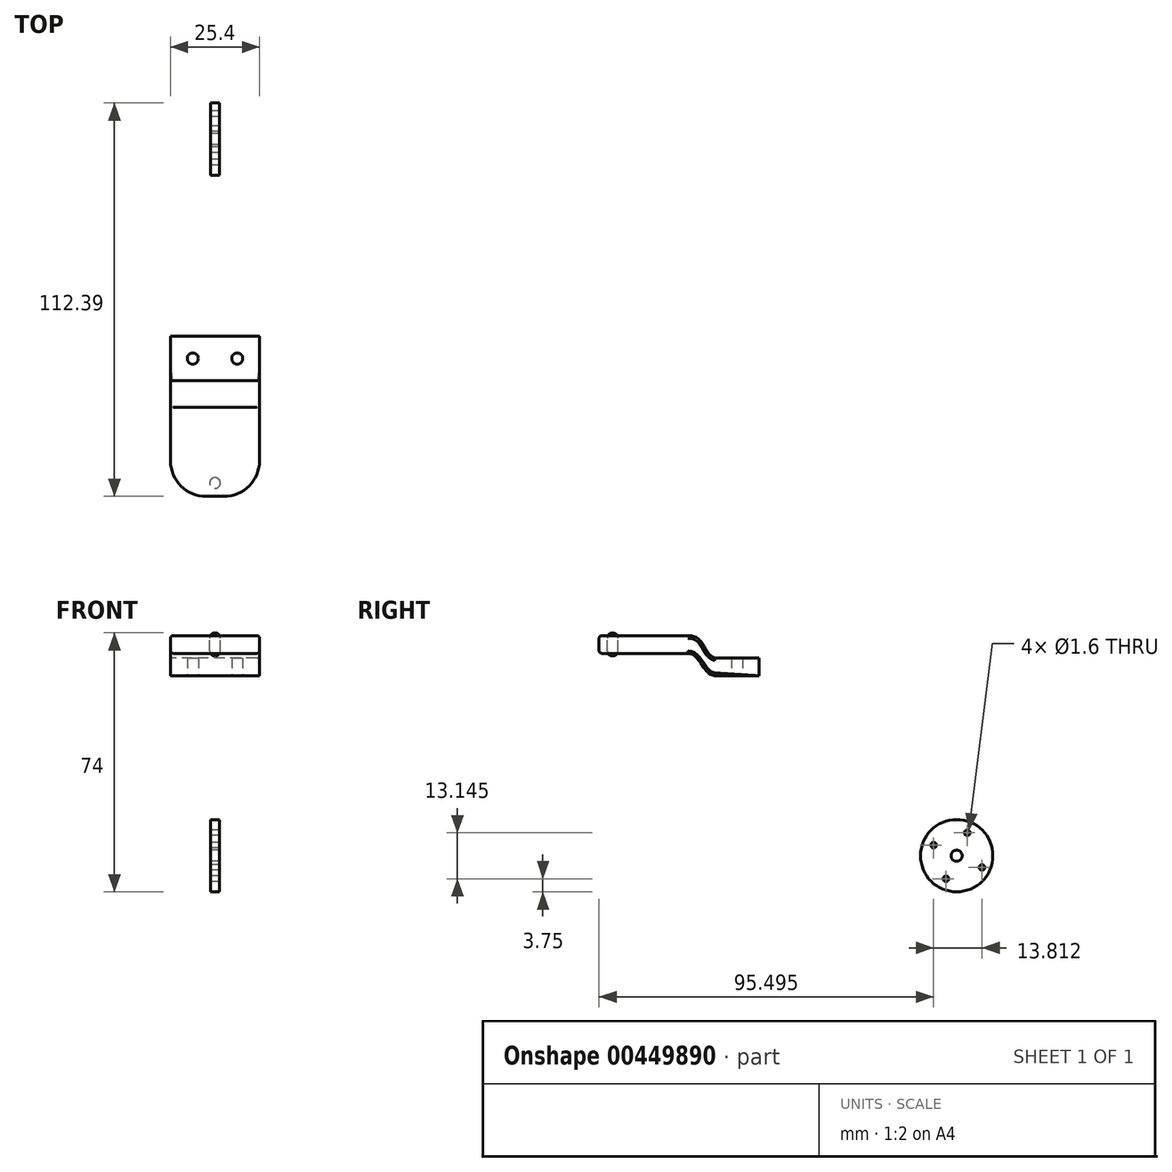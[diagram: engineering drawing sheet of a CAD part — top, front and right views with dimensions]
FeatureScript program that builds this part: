
annotation { "Feature Type Name" : "Feature", "Feature Type Description" : "" }
export const myFeature = defineFeature(function(context is Context, id is Id, definition is map)
    precondition{}
    {
        {
            var Q0;
            Q0=qCreatedBy(makeId("Right.planeOp"),FACE);
            var sketch = newSketch(context, id + "F0", { "sketchPlane" : qUnion([Q0])});
            skLineSegment(sketch, "E0.bottom", {"start": v(-34.21, 26.74) * mm, "end": v(-59.61, 26.74) * mm});
            skLineSegment(sketch, "E0.top", {"start": v(-34.21, 31.82) * mm, "end": v(-59.61, 31.82) * mm});
            skLineSegment(sketch, "E0.left", {"start": v(-34.21, 26.74) * mm, "end": v(-34.21, 31.82) * mm});
            skLineSegment(sketch, "E0.right", {"start": v(-59.61, 26.74) * mm, "end": v(-59.61, 31.82) * mm});
            skPoint(sketch, "E0.middle", {"position": v(-46.91, 29.28) * mm});
            skLineSegment(sketch, "E1.bottom", {"start": v(-13.9, 20.4) * mm, "end": v(-26.6, 20.4) * mm});
            skLineSegment(sketch, "E1.top", {"start": v(-13.9, 25.47) * mm, "end": v(-26.6, 25.47) * mm});
            skLineSegment(sketch, "E1.left", {"start": v(-13.9, 20.4) * mm, "end": v(-13.9, 25.47) * mm});
            skLineSegment(sketch, "E1.right", {"start": v(-26.6, 20.4) * mm, "end": v(-26.6, 25.47) * mm});
            skPoint(sketch, "E1.middle", {"position": v(-20.24, 22.93) * mm});
            skFitSpline(sketch, "E2", {"points": [v(-34.21, 31.82) * mm, v(-26.6, 25.47) * mm], "startDerivative": vector(14.44, 0.2) * mm, "endDerivative": vector(9.5, -2.66) * mm});
            skFitSpline(sketch, "E3", {"points": [v(-34.21, 26.74) * mm, v(-26.6, 20.4) * mm], "startDerivative": vector(10.36, -0.24) * mm, "endDerivative": vector(10.48, -0.64) * mm});
            skSolve(sketch);
        }
        {
            var Q0;
            Q0 = qSketchRegion(id + "F0", true);
            extrude(context, id + "F1", {"entities" : qUnion([Q0]), "endBound" : BoundingType.SYMMETRIC, "depth" : 25.4 * mm});
        }
        {
            var Q0;
            Q0=makeQuery(id+"F1.opExtrude","CAP_EDGE",EDGE,{"disambiguationData":[OSD([sQuery(id+"F0.wireOp",EDGE,"E0.right")])],"isStart":false});
            var Q1;
            Q1=makeQuery(id+"F1.opExtrude","CAP_EDGE",EDGE,{"disambiguationData":[OSD([sQuery(id+"F0.wireOp",EDGE,"E0.right")])],"isStart":true});
            fillet(context, id + "F2", {"entities" : qUnion([Q0, Q1]), "radius" : 10.16 * mm, "tangentPropagation" : true, "allowEdgeOverflow" : false});
        }
        {
            var Q0;
            Q0=makeQuery(id+"F1.opExtrude","CAP_EDGE",EDGE,{"disambiguationData":[OSD([sQuery(id+"F0.wireOp",EDGE,"E0.top")])],"isStart":false});
            var Q1;
            Q1=makeQuery(id+"F1.opExtrude","CAP_EDGE",EDGE,{"disambiguationData":[OSD([sQuery(id+"F0.wireOp",EDGE,"E1.top")])],"isStart":false});
            var Q2;
            Q2=makeQuery(id+"F1.opExtrude","CAP_EDGE",EDGE,{"disambiguationData":[OSD([sQuery(id+"F0.wireOp",EDGE,"E1.top")])],"isStart":true});
            var Q3;
            Q3=makeQuery(id+"F1.opExtrude","CAP_EDGE",EDGE,{"disambiguationData":[OSD([sQuery(id+"F0.wireOp",EDGE,"E0.bottom")])],"isStart":false});
            fillet(context, id + "F3", {"entities" : qUnion([Q0, Q1, Q2, Q3]), "radius" : 0.76 * mm, "tangentPropagation" : true, "allowEdgeOverflow" : false});
        }
        {
            var Q0;
            Q0=qCreatedBy(makeId("Top.planeOp"),FACE);
            var sketch = newSketch(context, id + "F4", { "sketchPlane" : qUnion([Q0])});
            skLineSegment(sketch, "E4", {"start": v(-22.65, -20.24) * mm, "end": v(23.2, -20.24) * mm});
            skCircle(sketch, "E5", {"center": v(-6.35, -20.24) * mm, "radius": 1.59 * mm});
            skCircle(sketch, "E6", {"center": v(6.35, -20.24) * mm, "radius": 1.59 * mm});
            skSolve(sketch);
        }
        {
            var Q0;
            Q0 = qSketchRegion(id + "F4", true);
            extrude(context, id + "F5", {"entities" : qUnion([Q0]), "operationType" : NewBodyOperationType.REMOVE, "depth" : 50.8 * mm});
        }
        {
            var Q0;
            Q0=qCreatedBy(makeId("Right.planeOp"),FACE);
            var sketch = newSketch(context, id + "F6", { "sketchPlane" : qUnion([Q0])});
            skPoint(sketch, "E7", {"position": v(-55.77, 31.06) * mm});
            skPoint(sketch, "E8", {"position": v(-55.77, 27.5) * mm});
            skArc(sketch, "E9", {"start": v(-55.77, 32.59) * mm, "mid": v(-54.7, 32.14) * mm, "end": v(-54.25, 31.06) * mm});
            skArc(sketch, "E10", {"start": v(-55.77, 25.98) * mm, "mid": v(-54.7, 26.43) * mm, "end": v(-54.25, 27.5) * mm});
            skLineSegment(sketch, "E11", {"start": v(-55.77, 32.59) * mm, "end": v(-55.77, 25.98) * mm});
            skLineSegment(sketch, "E12", {"start": v(-54.25, 31.06) * mm, "end": v(-54.25, 27.5) * mm});
            skLineSegment(sketch, "E13", {"start": v(-54.25, 29.28) * mm, "end": v(-55.77, 29.28) * mm});
            skSolve(sketch);
        }
        {
            var Q0;
            Q0 = qSketchRegion(id + "F6", true);
            var Q1;
            Q1=sQuery(id+"F6.wireOp",EDGE,"E11");
            revolve(context, id + "F7", {"entities" : qUnion([Q0]), "axis" : qUnion([Q1]), "revolveType" : RevolveType.FULL});
        }
        {
            var Q0;
            Q0=qCreatedBy(makeId("Right.planeOp"),FACE);
            var sketch = newSketch(context, id + "F8", { "sketchPlane" : qUnion([Q0])});
            skCircle(sketch, "E14", {"center": v(42.46, -31.09) * mm, "radius": 10.32 * mm});
            skCircle(sketch, "E15", {"center": v(42.46, -31.09) * mm, "radius": 1.59 * mm});
            skLineSegment(sketch, "E16", {"start": v(51.83, -35.41) * mm, "end": v(42.46, -31.09) * mm});
            skLineSegment(sketch, "E17", {"start": v(42.46, -31.09) * mm, "end": v(33.09, -26.76) * mm});
            skPoint(sketch, "E18", {"position": v(35.89, -28.05) * mm});
            skPoint(sketch, "E19", {"position": v(49.7, -34.43) * mm});
            skCircle(sketch, "E20", {"center": v(35.89, -28.05) * mm, "radius": 0.8 * mm});
            skCircle(sketch, "E21", {"center": v(49.7, -34.43) * mm, "radius": 0.8 * mm});
            skLineSegment(sketch, "E22", {"start": v(46.78, -21.72) * mm, "end": v(42.46, -31.09) * mm});
            skLineSegment(sketch, "E23", {"start": v(42.46, -31.09) * mm, "end": v(38.13, -40.46) * mm});
            skPoint(sketch, "E24", {"position": v(45.5, -24.51) * mm});
            skPoint(sketch, "E25", {"position": v(39.42, -37.66) * mm});
            skCircle(sketch, "E26", {"center": v(45.5, -24.51) * mm, "radius": 0.8 * mm});
            skCircle(sketch, "E27", {"center": v(39.42, -37.66) * mm, "radius": 0.8 * mm});
            skSolve(sketch);
        }
        {
            var Q0;
            Q0 = qSketchRegion(id + "F8", true);
            extrude(context, id + "F9", {"entities" : qUnion([Q0]), "endBound" : BoundingType.SYMMETRIC, "depth" : 2.54 * mm});
        }
    });
